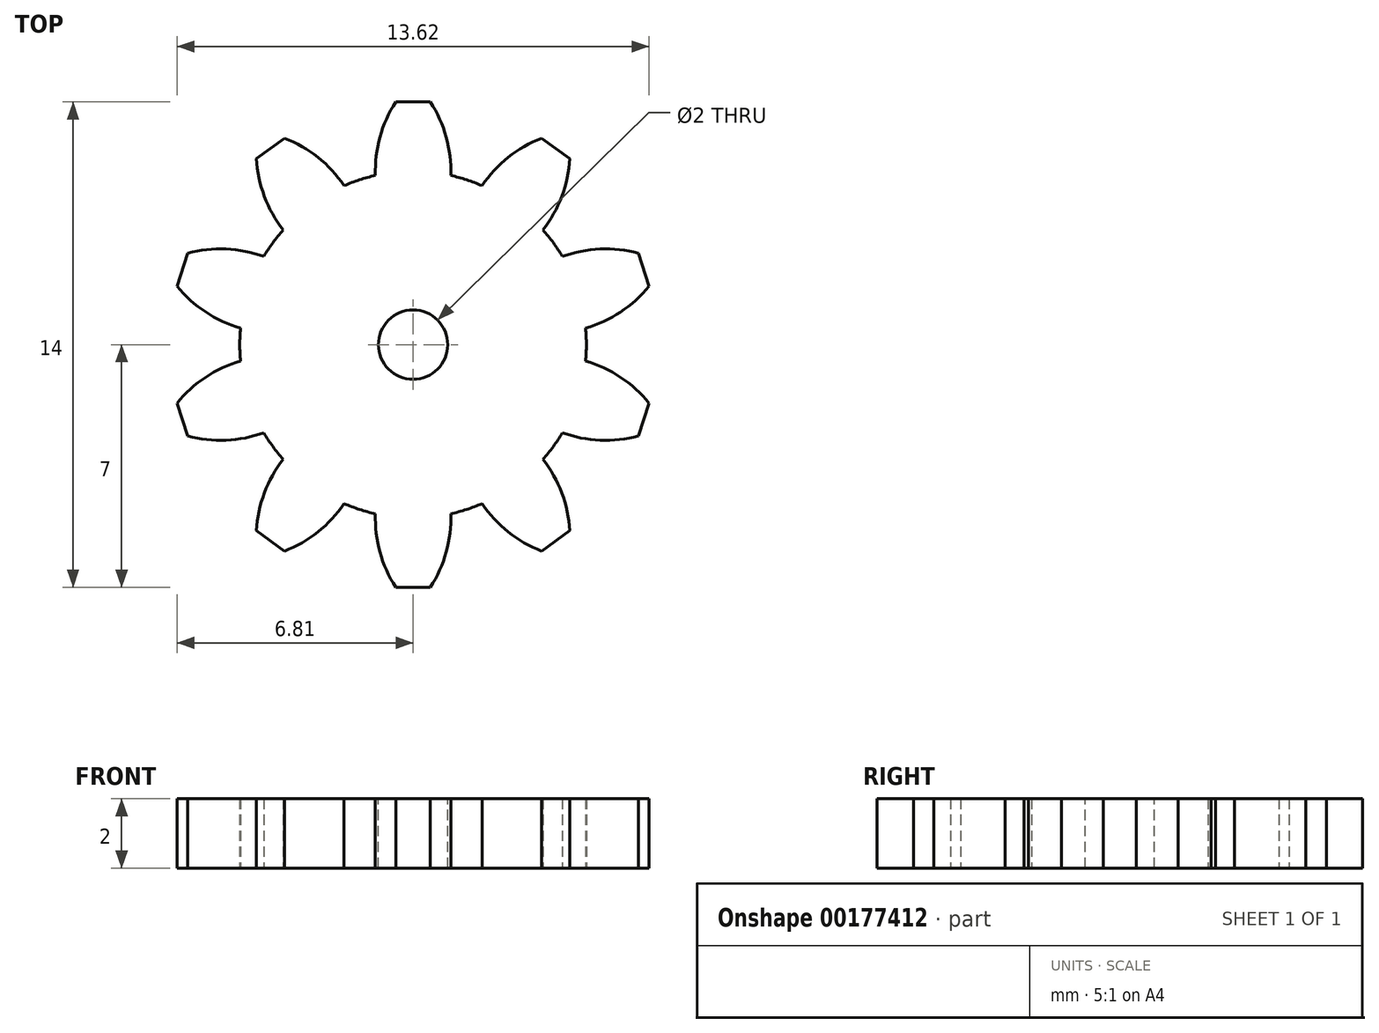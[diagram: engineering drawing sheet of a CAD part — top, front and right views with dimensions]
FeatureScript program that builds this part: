
annotation { "Feature Type Name" : "Feature", "Feature Type Description" : "" }
export const myFeature = defineFeature(function(context is Context, id is Id, definition is map)
    precondition{}
    {
        {
            var Q0;
            Q0=qCreatedBy(makeId("Top.planeOp"),FACE);
            var sketch = newSketch(context, id + "F0", { "sketchPlane" : qUnion([Q0])});
            skCircle(sketch, "E0", {"center": v(0, 0) * mm, "radius": 5 * mm});
            skLineSegment(sketch, "E1", {"start": v(0, 0) * mm, "end": v(0, 5) * mm, "construction": true});
            skLineSegment(sketch, "E2", {"start": v(0, 7) * mm, "end": v(-0.5, 7) * mm});
            skArc(sketch, "E3", {"start": v(-0.5, 7) * mm, "mid": v(-0.96, 5.98) * mm, "end": v(-1.09, 4.88) * mm});
            skLineSegment(sketch, "E4.MirrorCS", {"start": v(0, 7) * mm, "end": v(0.5, 7) * mm});
            skArc(sketch, "E5.MirrorCS", {"start": v(0.5, 7) * mm, "mid": v(0.96, 5.98) * mm, "end": v(1.09, 4.88) * mm});
            skArc(sketch, "E6.1.0", {"start": v(-4.52, 5.37) * mm, "mid": v(-4.3, 4.28) * mm, "end": v(-3.75, 3.3) * mm});
            skLineSegment(sketch, "E6.1.1", {"start": v(-4.11, 5.66) * mm, "end": v(-4.52, 5.37) * mm});
            skLineSegment(sketch, "E6.1.2", {"start": v(-4.11, 5.66) * mm, "end": v(-3.7, 5.96) * mm});
            skArc(sketch, "E6.1.3", {"start": v(-3.7, 5.96) * mm, "mid": v(-2.75, 5.4) * mm, "end": v(-1.99, 4.59) * mm});
            skArc(sketch, "E6.2.0", {"start": v(-6.81, 1.69) * mm, "mid": v(-5.99, 0.94) * mm, "end": v(-4.98, 0.47) * mm});
            skLineSegment(sketch, "E6.2.1", {"start": v(-6.66, 2.16) * mm, "end": v(-6.81, 1.69) * mm});
            skLineSegment(sketch, "E6.2.2", {"start": v(-6.66, 2.16) * mm, "end": v(-6.5, 2.64) * mm});
            skArc(sketch, "E6.2.3", {"start": v(-6.5, 2.64) * mm, "mid": v(-5.4, 2.76) * mm, "end": v(-4.3, 2.54) * mm});
            skArc(sketch, "E6.3.0", {"start": v(-6.5, -2.64) * mm, "mid": v(-5.4, -2.76) * mm, "end": v(-4.3, -2.54) * mm});
            skLineSegment(sketch, "E6.3.1", {"start": v(-6.66, -2.16) * mm, "end": v(-6.5, -2.64) * mm});
            skLineSegment(sketch, "E6.3.2", {"start": v(-6.66, -2.16) * mm, "end": v(-6.81, -1.69) * mm});
            skArc(sketch, "E6.3.3", {"start": v(-6.81, -1.69) * mm, "mid": v(-5.99, -0.94) * mm, "end": v(-4.98, -0.47) * mm});
            skArc(sketch, "E6.4.0", {"start": v(-3.7, -5.96) * mm, "mid": v(-2.75, -5.4) * mm, "end": v(-1.99, -4.59) * mm});
            skLineSegment(sketch, "E6.4.1", {"start": v(-4.11, -5.66) * mm, "end": v(-3.7, -5.96) * mm});
            skLineSegment(sketch, "E6.4.2", {"start": v(-4.11, -5.66) * mm, "end": v(-4.52, -5.37) * mm});
            skArc(sketch, "E6.4.3", {"start": v(-4.52, -5.37) * mm, "mid": v(-4.3, -4.28) * mm, "end": v(-3.75, -3.3) * mm});
            skArc(sketch, "E6.5.0", {"start": v(0.5, -7) * mm, "mid": v(0.96, -5.98) * mm, "end": v(1.09, -4.88) * mm});
            skLineSegment(sketch, "E6.5.1", {"start": v(0, -7) * mm, "end": v(0.5, -7) * mm});
            skLineSegment(sketch, "E6.5.2", {"start": v(0, -7) * mm, "end": v(-0.5, -7) * mm});
            skArc(sketch, "E6.5.3", {"start": v(-0.5, -7) * mm, "mid": v(-0.96, -5.98) * mm, "end": v(-1.09, -4.88) * mm});
            skArc(sketch, "E6.6.0", {"start": v(4.52, -5.37) * mm, "mid": v(4.3, -4.28) * mm, "end": v(3.75, -3.3) * mm});
            skLineSegment(sketch, "E6.6.1", {"start": v(4.11, -5.66) * mm, "end": v(4.52, -5.37) * mm});
            skLineSegment(sketch, "E6.6.2", {"start": v(4.11, -5.66) * mm, "end": v(3.7, -5.96) * mm});
            skArc(sketch, "E6.6.3", {"start": v(3.7, -5.96) * mm, "mid": v(2.75, -5.4) * mm, "end": v(1.99, -4.59) * mm});
            skArc(sketch, "E6.7.0", {"start": v(6.81, -1.69) * mm, "mid": v(5.99, -0.94) * mm, "end": v(4.98, -0.47) * mm});
            skLineSegment(sketch, "E6.7.1", {"start": v(6.66, -2.16) * mm, "end": v(6.81, -1.69) * mm});
            skLineSegment(sketch, "E6.7.2", {"start": v(6.66, -2.16) * mm, "end": v(6.5, -2.64) * mm});
            skArc(sketch, "E6.7.3", {"start": v(6.5, -2.64) * mm, "mid": v(5.4, -2.76) * mm, "end": v(4.3, -2.54) * mm});
            skArc(sketch, "E6.8.0", {"start": v(6.5, 2.64) * mm, "mid": v(5.4, 2.76) * mm, "end": v(4.3, 2.54) * mm});
            skLineSegment(sketch, "E6.8.1", {"start": v(6.66, 2.16) * mm, "end": v(6.5, 2.64) * mm});
            skLineSegment(sketch, "E6.8.2", {"start": v(6.66, 2.16) * mm, "end": v(6.81, 1.69) * mm});
            skArc(sketch, "E6.8.3", {"start": v(6.81, 1.69) * mm, "mid": v(5.99, 0.94) * mm, "end": v(4.98, 0.47) * mm});
            skArc(sketch, "E6.9.0", {"start": v(3.7, 5.96) * mm, "mid": v(2.75, 5.4) * mm, "end": v(1.99, 4.59) * mm});
            skLineSegment(sketch, "E6.9.1", {"start": v(4.11, 5.66) * mm, "end": v(3.7, 5.96) * mm});
            skLineSegment(sketch, "E6.9.2", {"start": v(4.11, 5.66) * mm, "end": v(4.52, 5.37) * mm});
            skArc(sketch, "E6.9.3", {"start": v(4.52, 5.37) * mm, "mid": v(4.3, 4.28) * mm, "end": v(3.75, 3.3) * mm});
            skSolve(sketch);
        }
        {
            var Q0;
            Q0=qSketchRegion(id+"F0",true);
            extrude(context, id + "F1", {"entities" : qUnion([Q0]), "depth" : 2 * mm});
        }
        {
            var Q0;
            Q0=makeQuery(id+"F1.opExtrude","CAP_FACE",FACE,{"disambiguationData":[OSD([sQuery(id+"F0.wireOp",EDGE,"E0"),sQuery(id+"F0.wireOp",EDGE,"E2"),sQuery(id+"F0.wireOp",EDGE,"E3"),sQuery(id+"F0.wireOp",EDGE,"E4.MirrorCS"),sQuery(id+"F0.wireOp",EDGE,"E5.MirrorCS"),sQuery(id+"F0.wireOp",EDGE,"E6.1.0"),sQuery(id+"F0.wireOp",EDGE,"E6.1.1"),sQuery(id+"F0.wireOp",EDGE,"E6.1.2"),sQuery(id+"F0.wireOp",EDGE,"E6.1.3"),sQuery(id+"F0.wireOp",EDGE,"E6.2.0"),sQuery(id+"F0.wireOp",EDGE,"E6.2.1"),sQuery(id+"F0.wireOp",EDGE,"E6.2.2"),sQuery(id+"F0.wireOp",EDGE,"E6.2.3"),sQuery(id+"F0.wireOp",EDGE,"E6.3.0"),sQuery(id+"F0.wireOp",EDGE,"E6.3.1"),sQuery(id+"F0.wireOp",EDGE,"E6.3.2"),sQuery(id+"F0.wireOp",EDGE,"E6.3.3"),sQuery(id+"F0.wireOp",EDGE,"E6.4.0"),sQuery(id+"F0.wireOp",EDGE,"E6.4.1"),sQuery(id+"F0.wireOp",EDGE,"E6.4.2"),sQuery(id+"F0.wireOp",EDGE,"E6.4.3"),sQuery(id+"F0.wireOp",EDGE,"E6.5.0"),sQuery(id+"F0.wireOp",EDGE,"E6.5.1"),sQuery(id+"F0.wireOp",EDGE,"E6.5.2"),sQuery(id+"F0.wireOp",EDGE,"E6.5.3"),sQuery(id+"F0.wireOp",EDGE,"E6.6.0"),sQuery(id+"F0.wireOp",EDGE,"E6.6.1"),sQuery(id+"F0.wireOp",EDGE,"E6.6.2"),sQuery(id+"F0.wireOp",EDGE,"E6.6.3"),sQuery(id+"F0.wireOp",EDGE,"E6.7.0"),sQuery(id+"F0.wireOp",EDGE,"E6.7.1"),sQuery(id+"F0.wireOp",EDGE,"E6.7.2"),sQuery(id+"F0.wireOp",EDGE,"E6.7.3"),sQuery(id+"F0.wireOp",EDGE,"E6.8.0"),sQuery(id+"F0.wireOp",EDGE,"E6.8.1"),sQuery(id+"F0.wireOp",EDGE,"E6.8.2"),sQuery(id+"F0.wireOp",EDGE,"E6.8.3"),sQuery(id+"F0.wireOp",EDGE,"E6.9.0"),sQuery(id+"F0.wireOp",EDGE,"E6.9.1"),sQuery(id+"F0.wireOp",EDGE,"E6.9.2"),sQuery(id+"F0.wireOp",EDGE,"E6.9.3"),sQuery(id+"F0.wireOp",EDGE,"E6.10.0"),sQuery(id+"F0.wireOp",EDGE,"E6.10.1"),sQuery(id+"F0.wireOp",EDGE,"E6.10.2"),sQuery(id+"F0.wireOp",EDGE,"E6.10.3"),sQuery(id+"F0.wireOp",EDGE,"E6.11.0"),sQuery(id+"F0.wireOp",EDGE,"E6.11.1"),sQuery(id+"F0.wireOp",EDGE,"E6.11.2"),sQuery(id+"F0.wireOp",EDGE,"E6.11.3"),sQuery(id+"F0.wireOp",EDGE,"E6.12.0"),sQuery(id+"F0.wireOp",EDGE,"E6.12.1"),sQuery(id+"F0.wireOp",EDGE,"E6.12.2"),sQuery(id+"F0.wireOp",EDGE,"E6.12.3"),sQuery(id+"F0.wireOp",EDGE,"E6.13.0"),sQuery(id+"F0.wireOp",EDGE,"E6.13.1"),sQuery(id+"F0.wireOp",EDGE,"E6.13.2"),sQuery(id+"F0.wireOp",EDGE,"E6.13.3"),sQuery(id+"F0.wireOp",EDGE,"E6.14.0"),sQuery(id+"F0.wireOp",EDGE,"E6.14.1"),sQuery(id+"F0.wireOp",EDGE,"E6.14.2"),sQuery(id+"F0.wireOp",EDGE,"E6.14.3"),sQuery(id+"F0.wireOp",EDGE,"E6.15.0"),sQuery(id+"F0.wireOp",EDGE,"E6.15.1"),sQuery(id+"F0.wireOp",EDGE,"E6.15.2"),sQuery(id+"F0.wireOp",EDGE,"E6.15.3")])],"isStart":false});
            var sketch = newSketch(context, id + "F2", { "sketchPlane" : qUnion([Q0])});
            skCircle(sketch, "E7", {"center": v(0, 0) * mm, "radius": 1 * mm});
            skSolve(sketch);
        }
        {
            var Q0;
            Q0=qSketchRegion(id+"F2",true);
            extrude(context, id + "F3", {"entities" : qUnion([Q0]), "operationType" : NewBodyOperationType.REMOVE, "endBound" : BoundingType.THROUGH_ALL, "oppositeDirection" : true, "depth" : 25 * mm});
        }
    });
